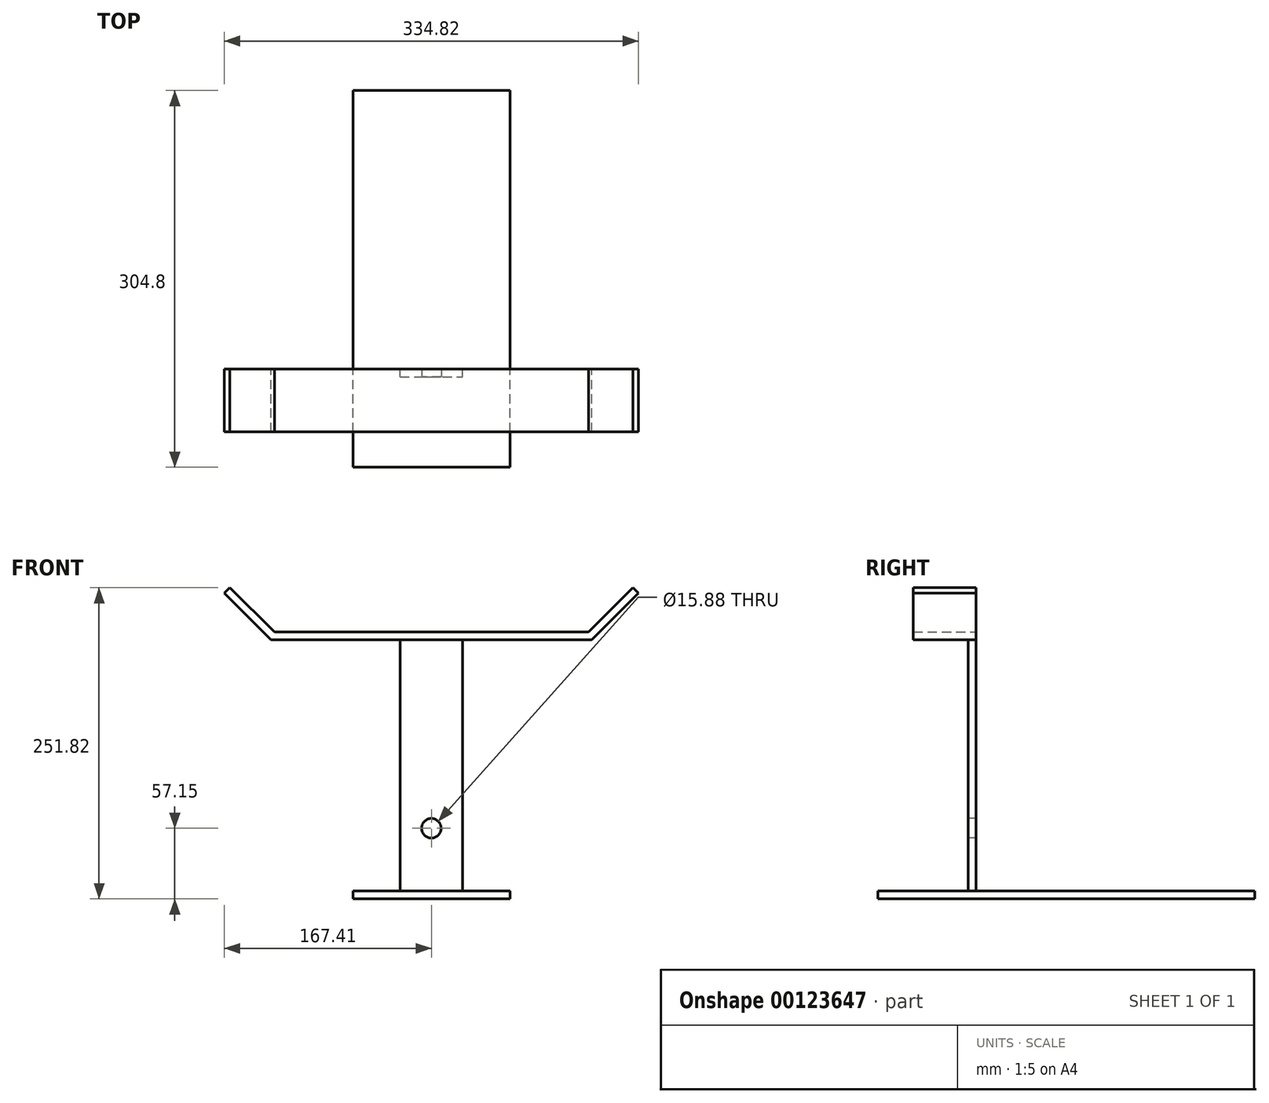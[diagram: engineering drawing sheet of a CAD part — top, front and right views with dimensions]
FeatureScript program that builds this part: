
annotation { "Feature Type Name" : "Feature", "Feature Type Description" : "" }
export const myFeature = defineFeature(function(context is Context, id is Id, definition is map)
    precondition{}
    {
        {
            var Q0;
            Q0=qCreatedBy(makeId("Top.planeOp"),FACE);
            var sketch = newSketch(context, id + "F0", { "sketchPlane" : qUnion([Q0])});
            skLineSegment(sketch, "E0.bottom", {"start": v(-63.5, -152.4) * mm, "end": v(63.5, -152.4) * mm});
            skLineSegment(sketch, "E0.top", {"start": v(-63.5, 152.4) * mm, "end": v(63.5, 152.4) * mm});
            skLineSegment(sketch, "E0.left", {"start": v(-63.5, -152.4) * mm, "end": v(-63.5, 152.4) * mm});
            skLineSegment(sketch, "E0.right", {"start": v(63.5, -152.4) * mm, "end": v(63.5, 152.4) * mm});
            skPoint(sketch, "E0.middle", {"position": v(0, 0) * mm});
            skSolve(sketch);
        }
        {
            var Q0;
            Q0 = qSketchRegion(id + "F0", true);
            extrude(context, id + "F1", {"entities" : qUnion([Q0]), "oppositeDirection" : true, "depth" : 6.35 * mm});
        }
        {
            var Q0;
            Q0=makeQuery(id+"F1.opExtrude","CAP_FACE",FACE,{"disambiguationData":[OSD([sQuery(id+"F0.wireOp",EDGE,"E0.bottom"),sQuery(id+"F0.wireOp",EDGE,"E0.top"),sQuery(id+"F0.wireOp",EDGE,"E0.left"),sQuery(id+"F0.wireOp",EDGE,"E0.right")])],"isStart":true});
            var sketch = newSketch(context, id + "F2", { "sketchPlane" : qUnion([Q0])});
            skLineSegment(sketch, "E1.bottom", {"start": v(-25.4, -79.38) * mm, "end": v(25.4, -79.38) * mm});
            skLineSegment(sketch, "E1.top", {"start": v(-25.4, -73.03) * mm, "end": v(25.4, -73.03) * mm});
            skLineSegment(sketch, "E1.left", {"start": v(-25.4, -79.38) * mm, "end": v(-25.4, -73.03) * mm});
            skLineSegment(sketch, "E1.right", {"start": v(25.4, -79.38) * mm, "end": v(25.4, -73.03) * mm});
            skPoint(sketch, "E1.middle", {"position": v(0, -76.2) * mm});
            skSolve(sketch);
        }
        {
            var Q0;
            Q0 = qSketchRegion(id + "F2", true);
            extrude(context, id + "F3", {"entities" : qUnion([Q0]), "operationType" : NewBodyOperationType.ADD, "depth" : 203.2 * mm});
        }
        {
            var Q0;
            Q0=makeQuery(id+"F3.opExtrude","SWEPT_FACE",FACE,{"disambiguationData":[OSD([sQuery(id+"F2.wireOp",EDGE,"E1.bottom")])]});
            var sketch = newSketch(context, id + "F4", { "sketchPlane" : qUnion([Q0])});
            skCircle(sketch, "E2", {"center": v(0, 50.8) * mm, "radius": 7.94 * mm});
            skSolve(sketch);
        }
        {
            var Q0;
            Q0=sQuery(id+"F4.wireOp",VERTEX,"E2.center");
            var Q1;
            Q1=makeQuery(id+"F1.opExtrude","SWEPT_BODY",BODY,{"disambiguationData":[OSD([sQuery(id+"F0.wireOp",EDGE,"E0.bottom"),sQuery(id+"F0.wireOp",EDGE,"E0.top"),sQuery(id+"F0.wireOp",EDGE,"E0.left"),sQuery(id+"F0.wireOp",EDGE,"E0.right")])]});
            hole(context, id + "F5", {"style" : HoleStyle.SIMPLE, "endStyle" : HoleEndStyle.THROUGH, "holeDiameter" : 15.88 * mm, "locations" : qUnion([Q0]), "scope" : qUnion([Q1]), "isTappedThrough" : true});
        }
        {
            var Q0;
            Q0=makeQuery(id+"F3.opExtrude","SWEPT_FACE",FACE,{"disambiguationData":[OSD([sQuery(id+"F2.wireOp",EDGE,"E1.top")])]});
            var sketch = newSketch(context, id + "F6", { "sketchPlane" : qUnion([Q0])});
            skLineSegment(sketch, "E3.bottom", {"start": v(-127, 203.2) * mm, "end": v(127, 203.2) * mm});
            skLineSegment(sketch, "E3.top", {"start": v(-127, 209.55) * mm, "end": v(127, 209.55) * mm});
            skPoint(sketch, "E3.middle", {"position": v(0, 206.38) * mm});
            skLineSegment(sketch, "E4", {"start": v(-127, 209.55) * mm, "end": v(-162.92, 245.47) * mm});
            skLineSegment(sketch, "E5", {"start": v(-162.92, 245.47) * mm, "end": v(-167.41, 240.98) * mm});
            skLineSegment(sketch, "E6", {"start": v(-167.41, 240.98) * mm, "end": v(-129.63, 203.2) * mm});
            skLineSegment(sketch, "E7", {"start": v(-129.63, 203.2) * mm, "end": v(-127, 203.2) * mm});
            skLineSegment(sketch, "E8.MirrorCS", {"start": v(129.63, 203.2) * mm, "end": v(127, 203.2) * mm});
            skLineSegment(sketch, "E9.MirrorCS", {"start": v(167.41, 240.98) * mm, "end": v(129.63, 203.2) * mm});
            skLineSegment(sketch, "E10.MirrorCS", {"start": v(127, 209.55) * mm, "end": v(162.92, 245.47) * mm});
            skLineSegment(sketch, "E11.MirrorCS", {"start": v(162.92, 245.47) * mm, "end": v(167.41, 240.98) * mm});
            skSolve(sketch);
        }
        {
            var Q0;
            Q0 = qSketchRegion(id + "F6", true);
            extrude(context, id + "F7", {"entities" : qUnion([Q0]), "operationType" : NewBodyOperationType.ADD, "oppositeDirection" : true, "depth" : 50.8 * mm});
        }
    });
